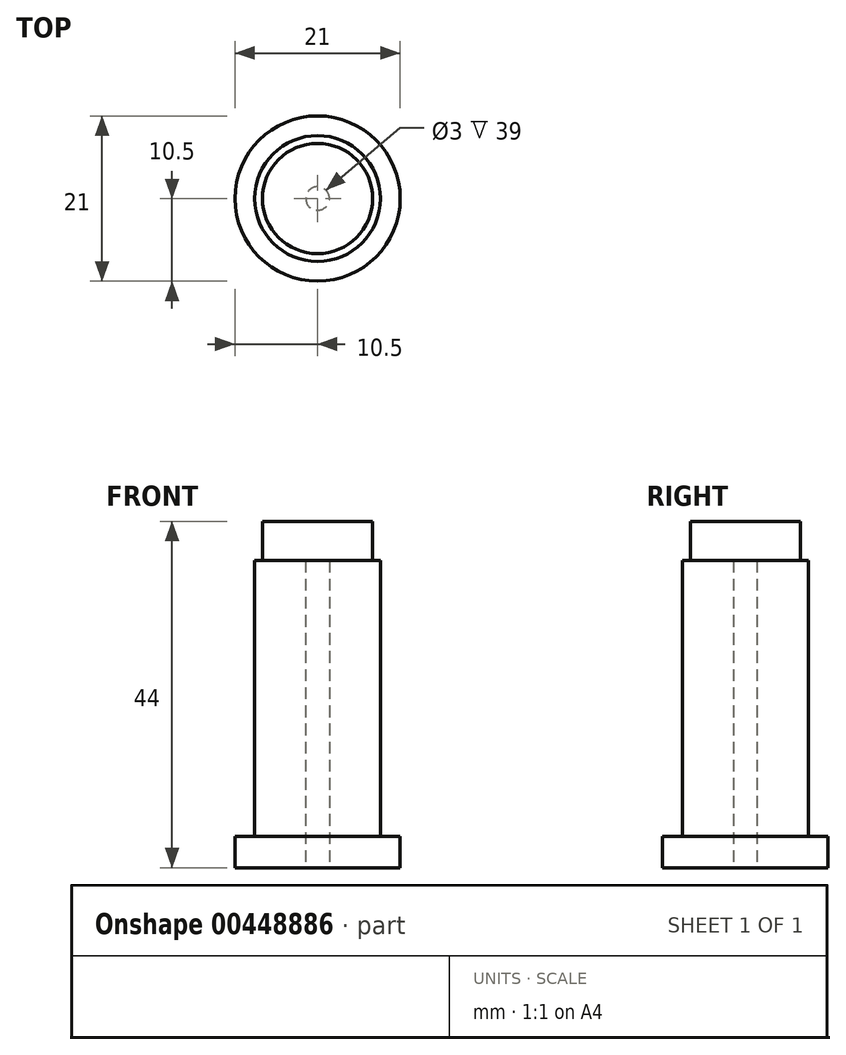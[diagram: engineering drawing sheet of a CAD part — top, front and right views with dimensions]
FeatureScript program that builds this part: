
annotation { "Feature Type Name" : "Feature", "Feature Type Description" : "" }
export const myFeature = defineFeature(function(context is Context, id is Id, definition is map)
    precondition{}
    {
        {
            var Q0;
            Q0=qCreatedBy(makeId("Top.planeOp"),FACE);
            var sketch = newSketch(context, id + "F0", { "sketchPlane" : qUnion([Q0])});
            skCircle(sketch, "E0", {"center": v(0, 0) * mm, "radius": 10.5 * mm});
            skSolve(sketch);
        }
        {
            var Q0;
            Q0=qSketchRegion(id+"F0",true);
            extrude(context, id + "F1", {"entities" : qUnion([Q0]), "depth" : 4 * mm});
        }
        {
            var Q0;
            Q0=qCreatedBy(makeId("Top.planeOp"),FACE);
            var sketch = newSketch(context, id + "F2", { "sketchPlane" : qUnion([Q0])});
            skCircle(sketch, "E1", {"center": v(0, 0) * mm, "radius": 8 * mm});
            skSolve(sketch);
        }
        {
            var Q0;
            Q0=qSketchRegion(id+"F2",true);
            extrude(context, id + "F3", {"entities" : qUnion([Q0]), "operationType" : NewBodyOperationType.ADD, "depth" : 39 * mm});
        }
        {
            var Q0;
            Q0=qCreatedBy(makeId("Right.planeOp"),FACE);
            var sketch = newSketch(context, id + "F4", { "sketchPlane" : qUnion([Q0])});
            skLineSegment(sketch, "E2", {"start": v(0, 44) * mm, "end": v(0, 39) * mm});
            skLineSegment(sketch, "E3", {"start": v(0, 39) * mm, "end": v(7, 39) * mm});
            skLineSegment(sketch, "E4", {"start": v(7, 39) * mm, "end": v(7, 44) * mm});
            skLineSegment(sketch, "E5", {"start": v(7, 44) * mm, "end": v(0, 44) * mm});
            skSolve(sketch);
        }
        {
            var Q0;
            Q0=makeQuery(id+"F4.imprint","IMPRINT",FACE,{"disambiguationData":[TD([[makeQuery(id+"F4.imprint","IMPRINT",EDGE,{"derivedFrom":sQuery(id+"F4.wireOp",EDGE,"E2")}),1.0]])]});
            var Q1;
            Q1=sQuery(id+"F4.wireOp",EDGE,"E2");
            revolve(context, id + "F5", {"operationType" : NewBodyOperationType.ADD, "entities" : qUnion([Q0]), "axis" : qUnion([Q1]), "revolveType" : RevolveType.FULL});
        }
        {
            var Q0;
            Q0=makeQuery(id+"F1.opExtrude","CAP_FACE",FACE,{"disambiguationData":[OSD([sQuery(id+"F0.wireOp",EDGE,"E0")])],"isStart":true});
            var sketch = newSketch(context, id + "F6", { "sketchPlane" : qUnion([Q0])});
            skCircle(sketch, "E6", {"center": v(0, 0) * mm, "radius": 1.5 * mm});
            skSolve(sketch);
        }
        {
            var Q0;
            Q0 = qSketchRegion(id + "F6", true);
            extrude(context, id + "F7", {"entities" : qUnion([Q0]), "operationType" : NewBodyOperationType.REMOVE, "oppositeDirection" : true, "depth" : 39 * mm});
        }
    });
